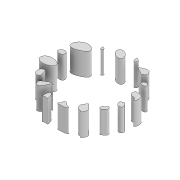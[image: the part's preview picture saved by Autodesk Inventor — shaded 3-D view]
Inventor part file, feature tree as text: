
AUTODESK INVENTOR PART (.ipt)
format: ipt  version: 2021 (Build 250183000, 183)  size: 243,712 bytes
history: native  units: in
note: dims shown in document units (in); Inventor stores cm internally (conversion verified against a paired STEP export)
features: extrude x1, mirror x1, sketch x1
ambient origin geometry x8: Origin, YZ Plane, XZ Plane, XY Plane, X Axis, Y Axis, Z Axis, Center Point
bodies: Body1 (feature_tree)
feature tree (3):
  extrude  "Extrusion2"  Depth=6.2992in TaperAngle=360.0deg
  mirror  "Mirror1"
  sketch  "Sketch1"  dims[d1=0.0773in d2=6.2992in d4=360.0deg d8=118.1102in d9=0.0in]
